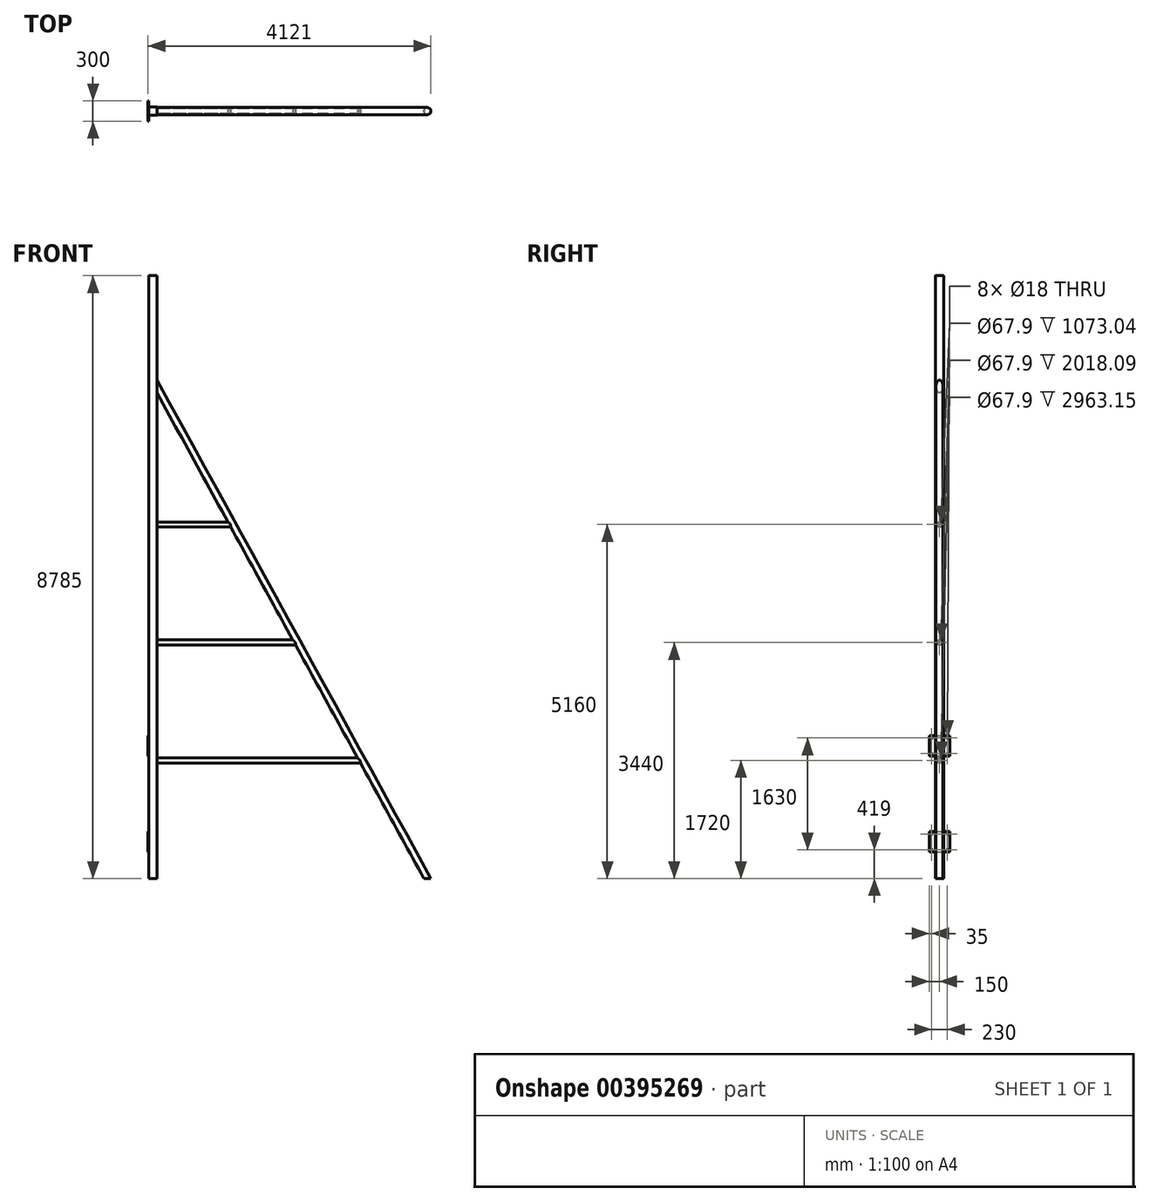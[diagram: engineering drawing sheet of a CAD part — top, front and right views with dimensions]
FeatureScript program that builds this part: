
annotation { "Feature Type Name" : "Feature", "Feature Type Description" : "" }
export const myFeature = defineFeature(function(context is Context, id is Id, definition is map)
    precondition{}
    {
        {
            var Q0;
            Q0=qCreatedBy(makeId("Top.planeOp"),FACE);
            var sketch = newSketch(context, id + "F0", { "sketchPlane" : qUnion([Q0])});
            skLineSegment(sketch, "E0.bottom", {"start": v(54, 60) * mm, "end": v(-54, 60) * mm});
            skLineSegment(sketch, "E0.top", {"start": v(54, -60) * mm, "end": v(-54, -60) * mm});
            skLineSegment(sketch, "E0.left", {"start": v(60, 54) * mm, "end": v(60, -54) * mm});
            skLineSegment(sketch, "E0.right", {"start": v(-60, 54) * mm, "end": v(-60, -54) * mm});
            skPoint(sketch, "E0.middle", {"position": v(0, 0) * mm});
            skLineSegment(sketch, "E1.0", {"start": v(51, 54) * mm, "end": v(-51, 54) * mm});
            skLineSegment(sketch, "E1.1", {"start": v(54, 51) * mm, "end": v(54, -51) * mm});
            skLineSegment(sketch, "E1.2", {"start": v(51, -54) * mm, "end": v(-51, -54) * mm});
            skLineSegment(sketch, "E1.3", {"start": v(-54, 51) * mm, "end": v(-54, -51) * mm});
            skPoint(sketch, "E2.visualSharp", {"position": v(-54, 54) * mm});
            skArc(sketch, "E2.filletArc", {"start": v(-51, 54) * mm, "mid": v(-53.12, 53.12) * mm, "end": v(-54, 51) * mm});
            skPoint(sketch, "E3.visualSharp", {"position": v(54, 54) * mm});
            skArc(sketch, "E3.filletArc", {"start": v(54, 51) * mm, "mid": v(53.12, 53.12) * mm, "end": v(51, 54) * mm});
            skPoint(sketch, "E4.visualSharp", {"position": v(54, -54) * mm});
            skArc(sketch, "E4.filletArc", {"start": v(51, -54) * mm, "mid": v(53.12, -53.12) * mm, "end": v(54, -51) * mm});
            skPoint(sketch, "E5.visualSharp", {"position": v(-54, -54) * mm});
            skArc(sketch, "E5.filletArc", {"start": v(-54, -51) * mm, "mid": v(-53.12, -53.12) * mm, "end": v(-51, -54) * mm});
            skPoint(sketch, "E6.visualSharp", {"position": v(60, -60) * mm});
            skArc(sketch, "E6.filletArc", {"start": v(54, -60) * mm, "mid": v(58.24, -58.24) * mm, "end": v(60, -54) * mm});
            skPoint(sketch, "E7.visualSharp", {"position": v(60, 60) * mm});
            skArc(sketch, "E7.filletArc", {"start": v(60, 54) * mm, "mid": v(58.24, 58.24) * mm, "end": v(54, 60) * mm});
            skPoint(sketch, "E8.visualSharp", {"position": v(-60, 60) * mm});
            skArc(sketch, "E8.filletArc", {"start": v(-54, 60) * mm, "mid": v(-58.24, 58.24) * mm, "end": v(-60, 54) * mm});
            skPoint(sketch, "E9.visualSharp", {"position": v(-60, -60) * mm});
            skArc(sketch, "E9.filletArc", {"start": v(-60, -54) * mm, "mid": v(-58.24, -58.24) * mm, "end": v(-54, -60) * mm});
            skSolve(sketch);
        }
        {
            var Q0;
            Q0 = qSketchRegion(id + "F0", true);
            extrude(context, id + "F1", {"entities" : qUnion([Q0]), "depth" : 8780 * mm});
        }
        {
            var Q0;
            Q0=qCreatedBy(makeId("Top.planeOp"),FACE);
            var sketch = newSketch(context, id + "F2", { "sketchPlane" : qUnion([Q0])});
            skCircle(sketch, "E10", {"center": v(4000, 0) * mm, "radius": 48.15 * mm});
            skCircle(sketch, "E11", {"center": v(4000, 0) * mm, "radius": 51 * mm});
            skSolve(sketch);
        }
        {
            var Q0;
            Q0=qCreatedBy(makeId("Front.planeOp"),FACE);
            var sketch = newSketch(context, id + "F3", { "sketchPlane" : qUnion([Q0])});
            skLineSegment(sketch, "E12", {"start": v(4000, 0) * mm, "end": v(0, 7280) * mm});
            skSolve(sketch);
        }
        {
            var Q0;
            Q0=makeQuery(id+"F2.imprint","IMPRINT",FACE,{"disambiguationData":[TD([[makeQuery(id+"F2.imprint","IMPRINT",EDGE,{"derivedFrom":sQuery(id+"F2.wireOp",EDGE,"E10")}),-1.0]])]});
            var Q1;
            Q1=sQuery(id+"F3.wireOp",EDGE,"E12");
            sweep(context, id + "F4", {"operationType" : NewBodyOperationType.ADD, "profiles" : qUnion([Q0]), "path" : qUnion([Q1])});
        }
        {
            var Q0;
            Q0=makeQuery(id+"F1.opExtrude","CAP_FACE",FACE,{"disambiguationData":[OSD([sQuery(id+"F0.wireOp",EDGE,"E0.bottom"),sQuery(id+"F0.wireOp",EDGE,"E0.top"),sQuery(id+"F0.wireOp",EDGE,"E0.left"),sQuery(id+"F0.wireOp",EDGE,"E0.right"),sQuery(id+"F0.wireOp",EDGE,"E1.0"),sQuery(id+"F0.wireOp",EDGE,"E1.1"),sQuery(id+"F0.wireOp",EDGE,"E1.2"),sQuery(id+"F0.wireOp",EDGE,"E1.3"),sQuery(id+"F0.wireOp",EDGE,"E2.filletArc"),sQuery(id+"F0.wireOp",EDGE,"E3.filletArc"),sQuery(id+"F0.wireOp",EDGE,"E4.filletArc"),sQuery(id+"F0.wireOp",EDGE,"E5.filletArc"),sQuery(id+"F0.wireOp",EDGE,"E6.filletArc"),sQuery(id+"F0.wireOp",EDGE,"E7.filletArc"),sQuery(id+"F0.wireOp",EDGE,"E8.filletArc"),sQuery(id+"F0.wireOp",EDGE,"E9.filletArc")])],"isStart":false});
            var sketch = newSketch(context, id + "F5", { "sketchPlane" : qUnion([Q0])});
            skLineSegment(sketch, "E13.0", {"start": v(51, -54) * mm, "end": v(-51, -54) * mm});
            skArc(sketch, "E13.1", {"start": v(51, -54) * mm, "mid": v(53.12, -53.12) * mm, "end": v(54, -51) * mm});
            skLineSegment(sketch, "E13.2", {"start": v(54, 51) * mm, "end": v(54, -51) * mm});
            skArc(sketch, "E13.3", {"start": v(54, 51) * mm, "mid": v(53.12, 53.12) * mm, "end": v(51, 54) * mm});
            skLineSegment(sketch, "E13.4", {"start": v(51, 54) * mm, "end": v(-51, 54) * mm});
            skArc(sketch, "E13.5", {"start": v(-51, 54) * mm, "mid": v(-53.12, 53.12) * mm, "end": v(-54, 51) * mm});
            skLineSegment(sketch, "E13.6", {"start": v(-54, 51) * mm, "end": v(-54, -51) * mm});
            skArc(sketch, "E13.7", {"start": v(-54, -51) * mm, "mid": v(-53.12, -53.12) * mm, "end": v(-51, -54) * mm});
            skSolve(sketch);
        }
        {
            var Q0;
            Q0 = qSketchRegion(id + "F5", true);
            extrude(context, id + "F6", {"entities" : qUnion([Q0]), "operationType" : NewBodyOperationType.REMOVE, "oppositeDirection" : true, "depth" : 2000 * mm});
        }
        {
            var Q0;
            Q0=makeQuery(id+"F1.opExtrude","CAP_FACE",FACE,{"disambiguationData":[OSD([sQuery(id+"F0.wireOp",EDGE,"E0.bottom"),sQuery(id+"F0.wireOp",EDGE,"E0.top"),sQuery(id+"F0.wireOp",EDGE,"E0.left"),sQuery(id+"F0.wireOp",EDGE,"E0.right"),sQuery(id+"F0.wireOp",EDGE,"E1.0"),sQuery(id+"F0.wireOp",EDGE,"E1.1"),sQuery(id+"F0.wireOp",EDGE,"E1.2"),sQuery(id+"F0.wireOp",EDGE,"E1.3"),sQuery(id+"F0.wireOp",EDGE,"E2.filletArc"),sQuery(id+"F0.wireOp",EDGE,"E3.filletArc"),sQuery(id+"F0.wireOp",EDGE,"E4.filletArc"),sQuery(id+"F0.wireOp",EDGE,"E5.filletArc"),sQuery(id+"F0.wireOp",EDGE,"E6.filletArc"),sQuery(id+"F0.wireOp",EDGE,"E7.filletArc"),sQuery(id+"F0.wireOp",EDGE,"E8.filletArc"),sQuery(id+"F0.wireOp",EDGE,"E9.filletArc")])],"isStart":false});
            var sketch = newSketch(context, id + "F7", { "sketchPlane" : qUnion([Q0])});
            skLineSegment(sketch, "E14.0", {"start": v(54, 60) * mm, "end": v(-54, 60) * mm});
            skArc(sketch, "E14.1", {"start": v(60, 54) * mm, "mid": v(58.24, 58.24) * mm, "end": v(54, 60) * mm});
            skLineSegment(sketch, "E14.2", {"start": v(60, 54) * mm, "end": v(60, -54) * mm});
            skArc(sketch, "E14.3", {"start": v(54, -60) * mm, "mid": v(58.24, -58.24) * mm, "end": v(60, -54) * mm});
            skLineSegment(sketch, "E14.4", {"start": v(54, -60) * mm, "end": v(-54, -60) * mm});
            skArc(sketch, "E14.5", {"start": v(-60, -54) * mm, "mid": v(-58.24, -58.24) * mm, "end": v(-54, -60) * mm});
            skLineSegment(sketch, "E14.6", {"start": v(-60, 54) * mm, "end": v(-60, -54) * mm});
            skArc(sketch, "E14.7", {"start": v(-54, 60) * mm, "mid": v(-58.24, 58.24) * mm, "end": v(-60, 54) * mm});
            skSolve(sketch);
        }
        {
            var Q0;
            Q0 = qSketchRegion(id + "F7", true);
            extrude(context, id + "F8", {"entities" : qUnion([Q0]), "operationType" : NewBodyOperationType.ADD, "depth" : 5 * mm});
        }
        {
            var Q0;
            {var subQ1=sQuery(id+"F0.wireOp",EDGE,"E6.filletArc");var subQ13=sQuery(id+"F0.wireOp",EDGE,"E0.left");Q0=makeQuery(id+"F8.boolean.opBoolean","MERGE",FACE,{"derivedFrom":[makeQuery(id+"F4.boolean.opBoolean","SPLIT",FACE,{"disambiguationData":[TD([makeQuery(id+"F1.opExtrude","SWEPT_FACE",FACE,{"disambiguationData":[OSD([subQ1])]})])],"derivedFrom":makeQuery(id+"F1.opExtrude","SWEPT_FACE",FACE,{"disambiguationData":[OSD([subQ13])]})}),makeQuery(id+"F8.opExtrude","SWEPT_FACE",FACE,{"disambiguationData":[OSD([sQuery(id+"F7.wireOp",EDGE,"E14.2")])]})]});}
            var sketch = newSketch(context, id + "F9", { "sketchPlane" : qUnion([Q0])});
            skCircle(sketch, "E15", {"center": v(0, 1720) * mm, "radius": 36.5 * mm});
            skCircle(sketch, "E16", {"center": v(0, 1720) * mm, "radius": 33.95 * mm});
            skCircle(sketch, "E17.0.1.0", {"center": v(0, 3440) * mm, "radius": 36.5 * mm});
            skCircle(sketch, "E17.0.1.1", {"center": v(0, 3440) * mm, "radius": 33.95 * mm});
            skCircle(sketch, "E17.0.2.0", {"center": v(0, 5160) * mm, "radius": 36.5 * mm});
            skCircle(sketch, "E17.0.2.1", {"center": v(0, 5160) * mm, "radius": 33.95 * mm});
            skLineSegment(sketch, "E17.direction1", {"start": v(0, 1720) * mm, "end": v(25, 1720) * mm, "construction": true});
            skLineSegment(sketch, "E17.direction2", {"start": v(0, 1720) * mm, "end": v(0, 3440) * mm, "construction": true});
            skSolve(sketch);
        }
        {
            var Q0;
            Q0 = qSketchRegion(id + "F9", true);
            extrude(context, id + "F10", {"entities" : qUnion([Q0]), "operationType" : NewBodyOperationType.ADD, "endBound" : BoundingType.UP_TO_NEXT, "depth" : 25 * mm});
        }
        {
            var Q0;
            Q0=makeQuery(id+"F8.boolean.opBoolean","MERGE",FACE,{"derivedFrom":[makeQuery(id+"F1.opExtrude","SWEPT_FACE",FACE,{"disambiguationData":[OSD([sQuery(id+"F0.wireOp",EDGE,"E0.right")])]}),makeQuery(id+"F8.opExtrude","SWEPT_FACE",FACE,{"disambiguationData":[OSD([sQuery(id+"F7.wireOp",EDGE,"E14.6")])]})]});
            var sketch = newSketch(context, id + "F11", { "sketchPlane" : qUnion([Q0])});
            skLineSegment(sketch, "E18.bottom", {"start": v(150, 684) * mm, "end": v(-150, 684) * mm});
            skLineSegment(sketch, "E18.top", {"start": v(150, 384) * mm, "end": v(-150, 384) * mm});
            skLineSegment(sketch, "E18.left", {"start": v(150, 684) * mm, "end": v(150, 384) * mm});
            skLineSegment(sketch, "E18.right", {"start": v(-150, 684) * mm, "end": v(-150, 384) * mm});
            skPoint(sketch, "E18.middle", {"position": v(0, 534) * mm});
            skLineSegment(sketch, "E19.direction1", {"start": v(-150, 384) * mm, "end": v(-125, 384) * mm, "construction": true});
            skCircle(sketch, "E20", {"center": v(-115, 649) * mm, "radius": 9 * mm});
            skCircle(sketch, "E21", {"center": v(115, 649) * mm, "radius": 9 * mm});
            skCircle(sketch, "E22", {"center": v(115, 419) * mm, "radius": 9 * mm});
            skCircle(sketch, "E23", {"center": v(-115, 419) * mm, "radius": 9 * mm});
            skLineSegment(sketch, "E24.0.1.0", {"start": v(-150, 2084) * mm, "end": v(-150, 1784) * mm});
            skLineSegment(sketch, "E24.0.1.1", {"start": v(150, 2084) * mm, "end": v(150, 1784) * mm});
            skPoint(sketch, "E24.0.1.2", {"position": v(0, 1934) * mm});
            skLineSegment(sketch, "E24.0.1.3", {"start": v(150, 1784) * mm, "end": v(-150, 1784) * mm});
            skLineSegment(sketch, "E24.0.1.4", {"start": v(150, 2084) * mm, "end": v(-150, 2084) * mm});
            skCircle(sketch, "E24.0.1.5", {"center": v(-115, 2049) * mm, "radius": 9 * mm});
            skCircle(sketch, "E24.0.1.6", {"center": v(115, 2049) * mm, "radius": 9 * mm});
            skCircle(sketch, "E24.0.1.7", {"center": v(115, 1819) * mm, "radius": 9 * mm});
            skLineSegment(sketch, "E24.0.1.8", {"start": v(-150, 1784) * mm, "end": v(-125, 1784) * mm, "construction": true});
            skCircle(sketch, "E24.0.1.9", {"center": v(-115, 1819) * mm, "radius": 9 * mm});
            skLineSegment(sketch, "E24.direction1", {"start": v(-150, 384) * mm, "end": v(-137.5, 384) * mm, "construction": true});
            skLineSegment(sketch, "E24.direction2", {"start": v(-150, 384) * mm, "end": v(-150, 1784) * mm, "construction": true});
            skSolve(sketch);
        }
        {
            var Q0;
            Q0 = qSketchRegion(id + "F11", true);
            extrude(context, id + "F12", {"entities" : qUnion([Q0]), "operationType" : NewBodyOperationType.ADD, "depth" : 10 * mm});
        }
    });
